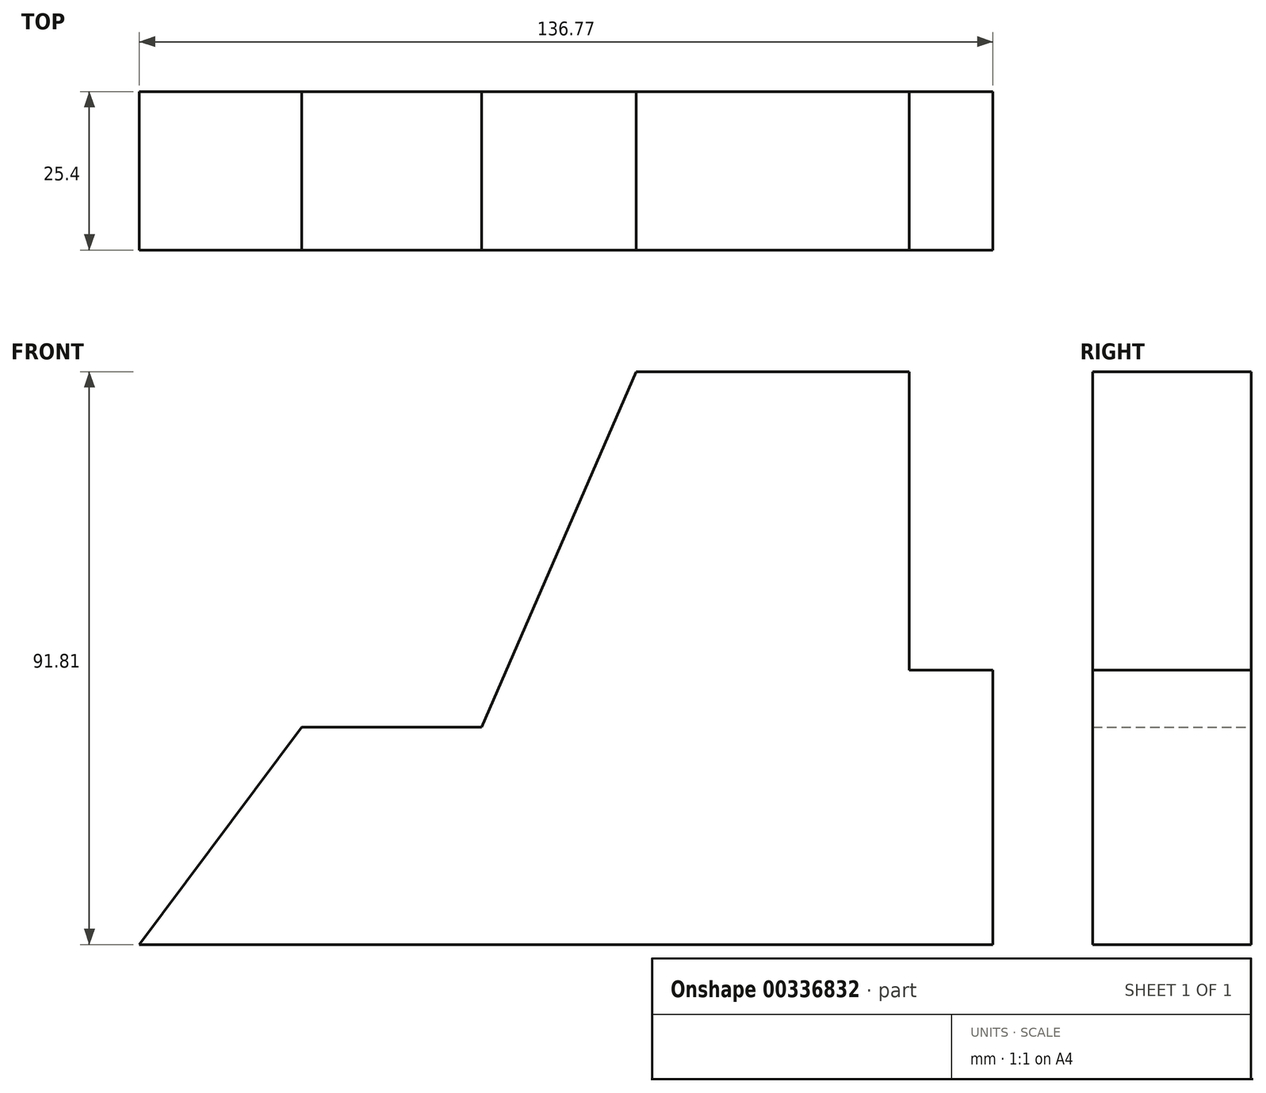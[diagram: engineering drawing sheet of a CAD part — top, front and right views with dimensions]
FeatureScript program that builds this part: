
annotation { "Feature Type Name" : "Feature", "Feature Type Description" : "" }
export const myFeature = defineFeature(function(context is Context, id is Id, definition is map)
    precondition{}
    {
        {
            var Q0;
            Q0=qCreatedBy(makeId("Front.planeOp"),FACE);
            var sketch = newSketch(context, id + "F0", { "sketchPlane" : qUnion([Q0])});
            skLineSegment(sketch, "E0", {"start": v(-70.3, -34.83) * mm, "end": v(-44.3, 0) * mm});
            skLineSegment(sketch, "E1", {"start": v(-70.3, -34.83) * mm, "end": v(66.46, -34.83) * mm});
            skLineSegment(sketch, "E2", {"start": v(66.46, -34.83) * mm, "end": v(66.46, 9.18) * mm});
            skLineSegment(sketch, "E3", {"start": v(66.46, 9.18) * mm, "end": v(53.05, 9.18) * mm});
            skLineSegment(sketch, "E4", {"start": v(53.05, 9.18) * mm, "end": v(53.05, 56.98) * mm});
            skLineSegment(sketch, "E5", {"start": v(53.05, 56.98) * mm, "end": v(9.33, 56.98) * mm});
            skLineSegment(sketch, "E6", {"start": v(9.33, 56.98) * mm, "end": v(-15.45, 0) * mm});
            skLineSegment(sketch, "E7", {"start": v(-15.45, 0) * mm, "end": v(-44.3, 0) * mm});
            skSolve(sketch);
        }
        {
            var Q0;
            Q0 = qSketchRegion(id + "F0", true);
            extrude(context, id + "F1", {"entities" : qUnion([Q0]), "depth" : 25.4 * mm});
        }
    });
